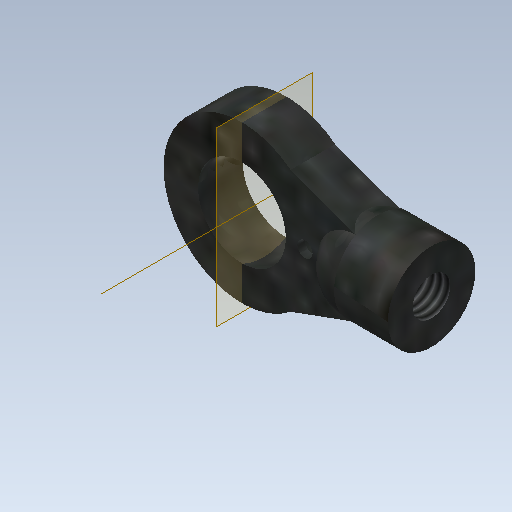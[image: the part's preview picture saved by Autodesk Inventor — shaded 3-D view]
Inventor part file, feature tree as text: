
AUTODESK INVENTOR PART (.ipt)
format: ipt  version: 2020 (Build 240168000, 168)  size: 192,512 bytes
history: native  units: mm
features: sketch x4, revolve x2, hole x2, projected_geometry x2, extrude x1, plane x1, other x1
ambient origin geometry x8: Origin, YZ Plane, XZ Plane, XY Plane, X Axis, Y Axis, Z Axis, Center Point
bodies: Solid1 (feature_tree)
feature tree (13):
  revolve  "Revolution1"  [1 undecoded]
  extrude  "Extrusion1"  Depth=10.2mm
  hole  "Hole1"  [1 undecoded]
  plane  "Work Plane1"
  revolve  "Revolution2"  [1 undecoded]
  hole  "Hole2"  [1 undecoded]
  sketch  "Sketch1"  dims[d0=2.85mm d1=3.5mm]
  sketch  "Sketch2"  dims[d2=90.0deg d3=10.2mm]
  other  "Work Axis1"
  sketch  "Sketch3"  dims[d4=10.9mm d7=8.0mm]
  sketch  "Sketch4"  dims[d10=2.9mm d11=0.0mm d12=19.198622mm d13=19.198622mm d23=10.0mm d24=10.0mm d16=2.459mm d17=5.0mm d18=4.0mm d19=2.0mm d20=90.0deg d21=6.0mm d22=20.594885mm d25=0.0mm d26=6.4mm d27=90.0deg d28=1.0mm d29=1.0mm d30=4.0mm d31=2.0mm d32=90.0deg d33=0.5mm d34=20.594885mm]
  projected_geometry  "Project Cut Edges1"
  projected_geometry  "Project Cut Edges2"
note: 4 required parameter values undecoded (feature->parameter linkage not recoverable at this tier; creation-order binding heuristic only, values carry confidence <= 0.55)